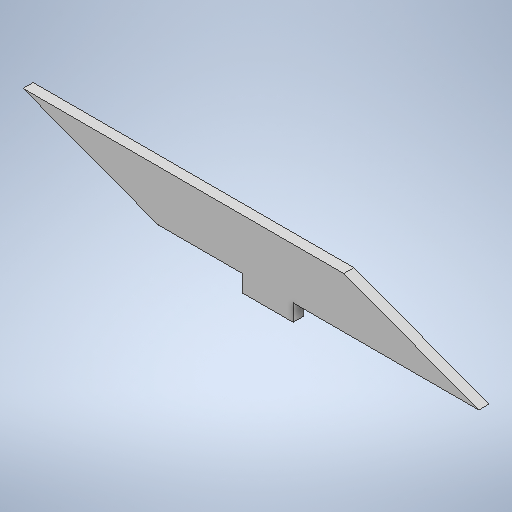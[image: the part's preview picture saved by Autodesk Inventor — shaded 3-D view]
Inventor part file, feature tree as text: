
AUTODESK INVENTOR PART (.ipt)
format: ipt  version: 2025.1 (Build 291241020, 241B)  size: 248,832 bytes
history: native  units: mm
features: extrude x1, sketch x1
ambient origin geometry x8: Origin, YZ Plane, XZ Plane, XY Plane, X Axis, Y Axis, Z Axis, Center Point
bodies: Solid1 (feature_tree)
feature tree (2):
  extrude  "Extrusion1"  Depth=3.0mm TaperAngle=0.0deg
  sketch  "Sketch1"  dims[d0=95.0mm d4=3.0mm d5=0.0mm d6=15.0mm d7=5.0mm d8=25.0mm d21=15.0mm d22=40.0mm]
